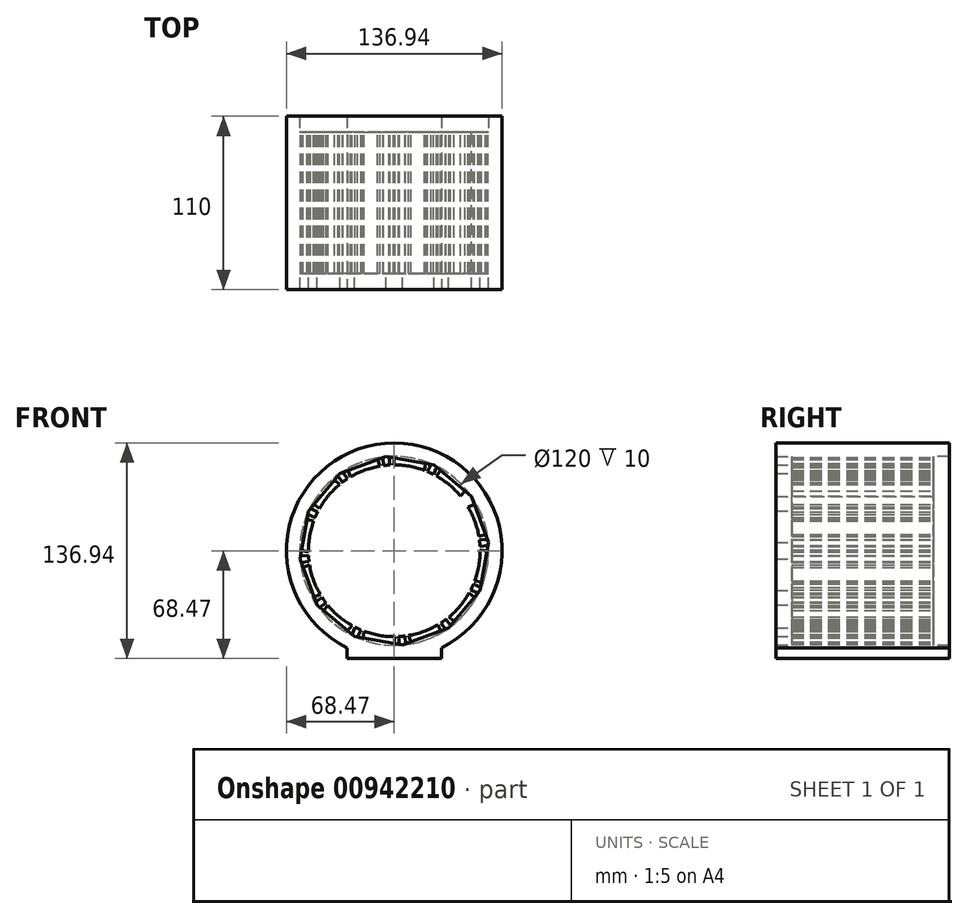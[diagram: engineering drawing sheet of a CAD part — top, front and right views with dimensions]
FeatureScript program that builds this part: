
annotation { "Feature Type Name" : "Feature", "Feature Type Description" : "" }
export const myFeature = defineFeature(function(context is Context, id is Id, definition is map)
    precondition{}
    {
        {
            var Q0;
            Q0=qCreatedBy(makeId("Front.planeOp"),FACE);
            var sketch = newSketch(context, id + "F0", { "sketchPlane" : qUnion([Q0])});
            skCircle(sketch, "E0.cCircle", {"center": v(0, 0) * mm, "radius": 60 * mm, "construction": true});
            skLineSegment(sketch, "E0.0", {"start": v(-54.41, 25.28) * mm, "end": v(-34.48, 49.1) * mm});
            skLineSegment(sketch, "E0.1", {"start": v(-34.48, 49.1) * mm, "end": v(-5.3, 59.76) * mm});
            skLineSegment(sketch, "E0.2", {"start": v(-5.3, 59.76) * mm, "end": v(25.28, 54.41) * mm});
            skLineSegment(sketch, "E0.3", {"start": v(25.28, 54.41) * mm, "end": v(49.1, 34.48) * mm});
            skLineSegment(sketch, "E0.4", {"start": v(49.1, 34.48) * mm, "end": v(59.76, 5.3) * mm});
            skLineSegment(sketch, "E0.5", {"start": v(59.76, 5.3) * mm, "end": v(54.41, -25.28) * mm});
            skLineSegment(sketch, "E0.6", {"start": v(54.41, -25.28) * mm, "end": v(34.48, -49.1) * mm});
            skLineSegment(sketch, "E0.7", {"start": v(34.48, -49.1) * mm, "end": v(5.3, -59.76) * mm});
            skLineSegment(sketch, "E0.8", {"start": v(5.3, -59.76) * mm, "end": v(-25.28, -54.41) * mm});
            skLineSegment(sketch, "E0.9", {"start": v(-25.28, -54.41) * mm, "end": v(-49.1, -34.48) * mm});
            skLineSegment(sketch, "E0.10", {"start": v(-49.1, -34.48) * mm, "end": v(-59.76, -5.3) * mm});
            skLineSegment(sketch, "E0.11", {"start": v(-59.76, -5.3) * mm, "end": v(-54.41, 25.28) * mm});
            skLineSegment(sketch, "E1", {"start": v(-34.2, 41.65) * mm, "end": v(-38.03, 44.86) * mm});
            skLineSegment(sketch, "E2", {"start": v(-47.03, 26.32) * mm, "end": v(-50.86, 29.52) * mm});
            skLineSegment(sketch, "E3", {"start": v(-34.2, 41.65) * mm, "end": v(-47.03, 26.32) * mm});
            skLineSegment(sketch, "E4", {"start": v(-4.76, 53.53) * mm, "end": v(5.3, -59.76) * mm, "construction": true});
            skLineSegment(sketch, "E5", {"start": v(-50.44, 18.98) * mm, "end": v(-55.37, 19.84) * mm});
            skLineSegment(sketch, "E6", {"start": v(-53.89, -0.73) * mm, "end": v(-58.81, 0.14) * mm});
            skLineSegment(sketch, "E7", {"start": v(-53.17, -8.79) * mm, "end": v(-57.87, -10.5) * mm});
            skLineSegment(sketch, "E8", {"start": v(-46.3, -27.57) * mm, "end": v(-51, -29.29) * mm});
            skLineSegment(sketch, "E9", {"start": v(-41.65, -34.2) * mm, "end": v(-44.86, -38.03) * mm});
            skLineSegment(sketch, "E10", {"start": v(-26.32, -47.03) * mm, "end": v(-29.52, -50.86) * mm});
            skLineSegment(sketch, "E11", {"start": v(-18.98, -50.44) * mm, "end": v(-19.84, -55.37) * mm});
            skLineSegment(sketch, "E12", {"start": v(0.73, -53.89) * mm, "end": v(-0.14, -58.81) * mm});
            skLineSegment(sketch, "E13", {"start": v(-8.79, 53.17) * mm, "end": v(-10.5, 57.87) * mm});
            skLineSegment(sketch, "E14", {"start": v(-27.57, 46.3) * mm, "end": v(-29.29, 51) * mm});
            skLineSegment(sketch, "E15.MirrorCS", {"start": v(-0.73, 53.89) * mm, "end": v(0.14, 58.81) * mm});
            skLineSegment(sketch, "E16.MirrorCS", {"start": v(18.98, 50.44) * mm, "end": v(19.84, 55.37) * mm});
            skLineSegment(sketch, "E17.MirrorCS", {"start": v(26.32, 47.03) * mm, "end": v(29.52, 50.86) * mm});
            skLineSegment(sketch, "E18.MirrorCS", {"start": v(26.32, 47.03) * mm, "end": v(41.65, 34.2) * mm});
            skLineSegment(sketch, "E19.MirrorCS", {"start": v(41.65, 34.2) * mm, "end": v(44.86, 38.03) * mm});
            skLineSegment(sketch, "E20.MirrorCS", {"start": v(46.3, 27.57) * mm, "end": v(51, 29.29) * mm});
            skLineSegment(sketch, "E21.MirrorCS", {"start": v(53.17, 8.79) * mm, "end": v(57.87, 10.5) * mm});
            skLineSegment(sketch, "E22.MirrorCS", {"start": v(53.89, 0.73) * mm, "end": v(58.81, -0.14) * mm});
            skLineSegment(sketch, "E23.MirrorCS", {"start": v(50.44, -18.98) * mm, "end": v(55.37, -19.84) * mm});
            skLineSegment(sketch, "E24.MirrorCS", {"start": v(47.03, -26.32) * mm, "end": v(50.86, -29.52) * mm});
            skLineSegment(sketch, "E25.MirrorCS", {"start": v(34.2, -41.65) * mm, "end": v(38.03, -44.86) * mm});
            skLineSegment(sketch, "E26.MirrorCS", {"start": v(27.57, -46.3) * mm, "end": v(29.29, -51) * mm});
            skLineSegment(sketch, "E27.MirrorCS", {"start": v(8.79, -53.17) * mm, "end": v(10.5, -57.87) * mm});
            skLineSegment(sketch, "E28", {"start": v(0.73, -53.89) * mm, "end": v(-18.98, -50.44) * mm});
            skLineSegment(sketch, "E29", {"start": v(-26.32, -47.03) * mm, "end": v(-41.65, -34.2) * mm});
            skLineSegment(sketch, "E30", {"start": v(-46.3, -27.57) * mm, "end": v(-53.17, -8.79) * mm});
            skLineSegment(sketch, "E31", {"start": v(-53.89, -0.73) * mm, "end": v(-50.44, 18.98) * mm});
            skLineSegment(sketch, "E32", {"start": v(-27.57, 46.3) * mm, "end": v(-8.79, 53.17) * mm});
            skPoint(sketch, "E33.MirrorCS.end.orphan", {"position": v(-0.73, 53.89) * mm});
            skPoint(sketch, "E34.MirrorCS.end.orphan", {"position": v(18.98, 50.44) * mm});
            skPoint(sketch, "E35.MirrorCS.end.orphan", {"position": v(46.3, 27.57) * mm});
            skPoint(sketch, "E36.MirrorCS.end.orphan", {"position": v(53.17, 8.79) * mm});
            skPoint(sketch, "E37.MirrorCS.end.orphan", {"position": v(53.89, 0.73) * mm});
            skPoint(sketch, "E38.MirrorCS.end.orphan", {"position": v(50.44, -18.98) * mm});
            skPoint(sketch, "E39.MirrorCS.end.orphan", {"position": v(47.03, -26.32) * mm});
            skPoint(sketch, "E40.MirrorCS.end.orphan", {"position": v(34.2, -41.65) * mm});
            skPoint(sketch, "E41.MirrorCS.end.orphan", {"position": v(27.57, -46.3) * mm});
            skPoint(sketch, "E42.MirrorCS.end.orphan", {"position": v(8.79, -53.17) * mm});
            skLineSegment(sketch, "E43", {"start": v(-0.73, 53.89) * mm, "end": v(18.98, 50.44) * mm});
            skLineSegment(sketch, "E44", {"start": v(46.3, 27.57) * mm, "end": v(53.17, 8.79) * mm});
            skLineSegment(sketch, "E45", {"start": v(53.89, 0.73) * mm, "end": v(50.44, -18.98) * mm});
            skLineSegment(sketch, "E46", {"start": v(47.03, -26.32) * mm, "end": v(34.2, -41.65) * mm});
            skLineSegment(sketch, "E47", {"start": v(27.57, -46.3) * mm, "end": v(8.79, -53.17) * mm});
            skCircle(sketch, "E48", {"center": v(0, 0) * mm, "radius": 60 * mm});
            skCircle(sketch, "E49", {"center": v(0, 0) * mm, "radius": 68.47 * mm});
            skLineSegment(sketch, "E50", {"start": v(-29.23, 45.14) * mm, "end": v(-30.88, 43.98) * mm});
            skLineSegment(sketch, "E51", {"start": v(-47.88, 24.48) * mm, "end": v(-48.73, 22.65) * mm});
            skLineSegment(sketch, "E52", {"start": v(-53.7, -2.74) * mm, "end": v(-53.53, -4.76) * mm});
            skLineSegment(sketch, "E53", {"start": v(-6.77, 53.35) * mm, "end": v(-4.76, 53.53) * mm});
            skLineSegment(sketch, "E54", {"start": v(-5.3, 59.76) * mm, "end": v(-4.76, 53.53) * mm});
            skLineSegment(sketch, "E55", {"start": v(20.81, 49.59) * mm, "end": v(22.65, 48.73) * mm});
            skLineSegment(sketch, "E56", {"start": v(42.82, 32.54) * mm, "end": v(43.98, 30.88) * mm});
            skLineSegment(sketch, "E57", {"start": v(5.3, -59.76) * mm, "end": v(4.76, -53.53) * mm});
            skLineSegment(sketch, "E58", {"start": v(-42.82, -32.54) * mm, "end": v(-43.98, -30.88) * mm});
            skLineSegment(sketch, "E59", {"start": v(-43.98, -30.88) * mm, "end": v(-45.14, -29.23) * mm});
            skLineSegment(sketch, "E60", {"start": v(43.98, 30.88) * mm, "end": v(45.14, 29.23) * mm});
            skLineSegment(sketch, "E61", {"start": v(22.65, 48.73) * mm, "end": v(24.48, 47.88) * mm});
            skLineSegment(sketch, "E62", {"start": v(-4.76, 53.53) * mm, "end": v(-2.74, 53.7) * mm});
            skLineSegment(sketch, "E63", {"start": v(-30.88, 43.98) * mm, "end": v(-32.54, 42.82) * mm});
            skLineSegment(sketch, "E64", {"start": v(-48.73, 22.65) * mm, "end": v(-49.59, 20.81) * mm});
            skLineSegment(sketch, "E65", {"start": v(-47.88, 24.48) * mm, "end": v(-53.07, 26.9) * mm});
            skLineSegment(sketch, "E66.MirrorCS", {"start": v(-49.59, 20.81) * mm, "end": v(-54.77, 23.22) * mm});
            skPoint(sketch, "E67.end.orphan", {"position": v(-48.73, 22.65) * mm});
            skLineSegment(sketch, "E68", {"start": v(-53.53, -4.76) * mm, "end": v(-53.35, -6.77) * mm});
            skLineSegment(sketch, "E69", {"start": v(-53.7, -2.74) * mm, "end": v(-59.4, -3.25) * mm});
            skLineSegment(sketch, "E70.MirrorCS", {"start": v(-53.35, -6.77) * mm, "end": v(-59.05, -7.28) * mm});
            skPoint(sketch, "E71.end.orphan", {"position": v(-53.53, -4.76) * mm});
            skLineSegment(sketch, "E72", {"start": v(-45.14, -29.23) * mm, "end": v(-49.82, -32.51) * mm});
            skLineSegment(sketch, "E73.MirrorCS", {"start": v(-42.82, -32.54) * mm, "end": v(-47.5, -35.83) * mm});
            skPoint(sketch, "E74.end.orphan", {"position": v(-43.98, -30.88) * mm});
            skLineSegment(sketch, "E75", {"start": v(-32.54, 42.82) * mm, "end": v(-35.83, 47.5) * mm});
            skLineSegment(sketch, "E76.MirrorCS", {"start": v(-29.23, 45.14) * mm, "end": v(-32.51, 49.82) * mm});
            skPoint(sketch, "E77.end.orphan", {"position": v(-30.88, 43.98) * mm});
            skLineSegment(sketch, "E78", {"start": v(-6.77, 53.35) * mm, "end": v(-7.28, 59.05) * mm});
            skLineSegment(sketch, "E79.MirrorCS", {"start": v(-2.74, 53.7) * mm, "end": v(-3.25, 59.4) * mm});
            skLineSegment(sketch, "E80", {"start": v(20.81, 49.59) * mm, "end": v(23.22, 54.77) * mm});
            skLineSegment(sketch, "E81.MirrorCS", {"start": v(24.48, 47.88) * mm, "end": v(26.9, 53.07) * mm});
            skPoint(sketch, "E82.end.orphan", {"position": v(22.65, 48.73) * mm});
            skLineSegment(sketch, "E83", {"start": v(42.82, 32.54) * mm, "end": v(47.5, 35.83) * mm});
            skLineSegment(sketch, "E84.MirrorCS", {"start": v(45.14, 29.23) * mm, "end": v(49.82, 32.51) * mm});
            skPoint(sketch, "E85.end.orphan", {"position": v(43.98, 30.88) * mm});
            skLineSegment(sketch, "E86.MirrorCS", {"start": v(53.35, 6.77) * mm, "end": v(59.05, 7.28) * mm});
            skLineSegment(sketch, "E87.MirrorCS", {"start": v(53.7, 2.74) * mm, "end": v(59.4, 3.25) * mm});
            skLineSegment(sketch, "E88.MirrorCS", {"start": v(53.53, 4.76) * mm, "end": v(53.7, 2.74) * mm});
            skLineSegment(sketch, "E89.MirrorCS", {"start": v(53.35, 6.77) * mm, "end": v(53.53, 4.76) * mm});
            skLineSegment(sketch, "E90", {"start": v(-20.81, -49.59) * mm, "end": v(-22.65, -48.73) * mm});
            skLineSegment(sketch, "E91", {"start": v(-22.65, -48.73) * mm, "end": v(-26.32, -47.03) * mm});
            skLineSegment(sketch, "E92", {"start": v(59.76, 5.3) * mm, "end": v(-59.76, -5.3) * mm, "construction": true});
            skLineSegment(sketch, "E93.MirrorCS", {"start": v(6.77, -53.35) * mm, "end": v(7.28, -59.05) * mm});
            skLineSegment(sketch, "E94.MirrorCS", {"start": v(2.74, -53.7) * mm, "end": v(3.25, -59.4) * mm});
            skLineSegment(sketch, "E95.MirrorCS", {"start": v(2.74, -53.7) * mm, "end": v(4.76, -53.53) * mm});
            skLineSegment(sketch, "E96.MirrorCS", {"start": v(4.76, -53.53) * mm, "end": v(6.77, -53.35) * mm});
            skLineSegment(sketch, "E97.MirrorCS", {"start": v(-20.81, -49.59) * mm, "end": v(-23.22, -54.77) * mm});
            skLineSegment(sketch, "E98.MirrorCS", {"start": v(-24.48, -47.88) * mm, "end": v(-26.9, -53.07) * mm});
            skLineSegment(sketch, "E99", {"start": v(49.1, 34.48) * mm, "end": v(-49.1, -34.48) * mm, "construction": true});
            skLineSegment(sketch, "E100", {"start": v(-54.41, 25.28) * mm, "end": v(54.41, -25.28) * mm, "construction": true});
            skLineSegment(sketch, "E101", {"start": v(25.28, 54.41) * mm, "end": v(-25.28, -54.41) * mm, "construction": true});
            skLineSegment(sketch, "E102", {"start": v(34.48, -49.1) * mm, "end": v(-34.48, 49.1) * mm, "construction": true});
            skLineSegment(sketch, "E103.MirrorCS", {"start": v(29.23, -45.14) * mm, "end": v(32.51, -49.82) * mm});
            skLineSegment(sketch, "E104.MirrorCS", {"start": v(32.54, -42.82) * mm, "end": v(35.83, -47.5) * mm});
            skPoint(sketch, "E105.MirrorP", {"position": v(30.88, -43.98) * mm});
            skLineSegment(sketch, "E106.MirrorCS", {"start": v(30.88, -43.98) * mm, "end": v(29.23, -45.14) * mm});
            skLineSegment(sketch, "E107.MirrorCS", {"start": v(32.54, -42.82) * mm, "end": v(30.88, -43.98) * mm});
            skLineSegment(sketch, "E108.MirrorCS", {"start": v(49.59, -20.81) * mm, "end": v(54.77, -23.22) * mm});
            skLineSegment(sketch, "E109.MirrorCS", {"start": v(47.88, -24.48) * mm, "end": v(53.07, -26.9) * mm});
            skLineSegment(sketch, "E110.MirrorCS", {"start": v(48.73, -22.65) * mm, "end": v(47.88, -24.48) * mm});
            skLineSegment(sketch, "E111.MirrorCS", {"start": v(49.59, -20.81) * mm, "end": v(48.73, -22.65) * mm});
            skSolve(sketch);
        }
        {
            var Q0;
            Q0=makeQuery(id+"F0.imprint","IMPRINT",FACE,{"disambiguationData":[TD([[makeQuery(id+"F0.imprint","IMPRINT",EDGE,{"derivedFrom":sQuery(id+"F0.wireOp",EDGE,"E49")}),1.0]])]});
            var Q1;
            {var subQ0=sQuery(id+"F0.wireOp",EDGE,"E0.11");var subQ3=makeQuery(id+"F0.imprint","INTERSECT",VERTEX,{"derivedFrom":[subQ0,sQuery(id+"F0.wireOp",EDGE,"E6")]});Q1=makeQuery(id+"F0.imprint","IMPRINT",FACE,{"disambiguationData":[TD([[makeQuery(id+"F0.imprint","IMPRINT",EDGE,{"disambiguationData":[TD([[subQ3,1.0]])],"derivedFrom":subQ0}),1.0]])]});}
            var Q2;
            {var subQ0=sQuery(id+"F0.wireOp",EDGE,"E0.10");var subQ3=makeQuery(id+"F0.imprint","INTERSECT",VERTEX,{"derivedFrom":[subQ0,sQuery(id+"F0.wireOp",EDGE,"E8")]});Q2=makeQuery(id+"F0.imprint","IMPRINT",FACE,{"disambiguationData":[TD([[makeQuery(id+"F0.imprint","IMPRINT",EDGE,{"disambiguationData":[TD([[subQ3,1.0]])],"derivedFrom":subQ0}),1.0]])]});}
            var Q3;
            {var subQ0=sQuery(id+"F0.wireOp",EDGE,"E0.9");var subQ3=makeQuery(id+"F0.imprint","INTERSECT",VERTEX,{"derivedFrom":[subQ0,sQuery(id+"F0.wireOp",EDGE,"E10")]});Q3=makeQuery(id+"F0.imprint","IMPRINT",FACE,{"disambiguationData":[TD([[makeQuery(id+"F0.imprint","IMPRINT",EDGE,{"disambiguationData":[TD([[subQ3,1.0]])],"derivedFrom":subQ0}),1.0]])]});}
            var Q4;
            {var subQ0=sQuery(id+"F0.wireOp",EDGE,"E0.8");var subQ3=makeQuery(id+"F0.imprint","INTERSECT",VERTEX,{"derivedFrom":[subQ0,sQuery(id+"F0.wireOp",EDGE,"E12")]});Q4=makeQuery(id+"F0.imprint","IMPRINT",FACE,{"disambiguationData":[TD([[makeQuery(id+"F0.imprint","IMPRINT",EDGE,{"disambiguationData":[TD([[subQ3,1.0]])],"derivedFrom":subQ0}),1.0]])]});}
            var Q5;
            {var subQ0=sQuery(id+"F0.wireOp",EDGE,"E0.7");var subQ6=makeQuery(id+"F0.imprint","INTERSECT",VERTEX,{"derivedFrom":[subQ0,sQuery(id+"F0.wireOp",EDGE,"E26.MirrorCS")]});Q5=makeQuery(id+"F0.imprint","IMPRINT",FACE,{"disambiguationData":[TD([[makeQuery(id+"F0.imprint","IMPRINT",EDGE,{"disambiguationData":[TD([[subQ6,1.0]])],"derivedFrom":subQ0}),1.0]])]});}
            var Q6;
            {var subQ0=sQuery(id+"F0.wireOp",EDGE,"E0.6");var subQ3=makeQuery(id+"F0.imprint","INTERSECT",VERTEX,{"derivedFrom":[subQ0,sQuery(id+"F0.wireOp",EDGE,"E24.MirrorCS")]});Q6=makeQuery(id+"F0.imprint","IMPRINT",FACE,{"disambiguationData":[TD([[makeQuery(id+"F0.imprint","IMPRINT",EDGE,{"disambiguationData":[TD([[subQ3,1.0]])],"derivedFrom":subQ0}),1.0]])]});}
            var Q7;
            {var subQ0=sQuery(id+"F0.wireOp",EDGE,"E0.5");var subQ3=makeQuery(id+"F0.imprint","INTERSECT",VERTEX,{"derivedFrom":[subQ0,sQuery(id+"F0.wireOp",EDGE,"E22.MirrorCS")]});Q7=makeQuery(id+"F0.imprint","IMPRINT",FACE,{"disambiguationData":[TD([[makeQuery(id+"F0.imprint","IMPRINT",EDGE,{"disambiguationData":[TD([[subQ3,1.0]])],"derivedFrom":subQ0}),1.0]])]});}
            var Q8;
            {var subQ0=sQuery(id+"F0.wireOp",EDGE,"E0.0");var subQ3=makeQuery(id+"F0.imprint","INTERSECT",VERTEX,{"derivedFrom":[subQ0,sQuery(id+"F0.wireOp",EDGE,"E2")]});Q8=makeQuery(id+"F0.imprint","IMPRINT",FACE,{"disambiguationData":[TD([[makeQuery(id+"F0.imprint","IMPRINT",EDGE,{"disambiguationData":[TD([[subQ3,1.0]])],"derivedFrom":subQ0}),1.0]])]});}
            var Q9;
            {var subQ0=sQuery(id+"F0.wireOp",EDGE,"E0.1");var subQ3=makeQuery(id+"F0.imprint","INTERSECT",VERTEX,{"derivedFrom":[subQ0,sQuery(id+"F0.wireOp",EDGE,"E14")]});Q9=makeQuery(id+"F0.imprint","IMPRINT",FACE,{"disambiguationData":[TD([[makeQuery(id+"F0.imprint","IMPRINT",EDGE,{"disambiguationData":[TD([[subQ3,1.0]])],"derivedFrom":subQ0}),1.0]])]});}
            var Q10;
            {var subQ0=sQuery(id+"F0.wireOp",EDGE,"E0.2");var subQ3=makeQuery(id+"F0.imprint","INTERSECT",VERTEX,{"derivedFrom":[subQ0,sQuery(id+"F0.wireOp",EDGE,"E15.MirrorCS")]});Q10=makeQuery(id+"F0.imprint","IMPRINT",FACE,{"disambiguationData":[TD([[makeQuery(id+"F0.imprint","IMPRINT",EDGE,{"disambiguationData":[TD([[subQ3,1.0]])],"derivedFrom":subQ0}),1.0]])]});}
            var Q11;
            {var subQ0=sQuery(id+"F0.wireOp",EDGE,"E0.3");var subQ3=makeQuery(id+"F0.imprint","INTERSECT",VERTEX,{"derivedFrom":[subQ0,sQuery(id+"F0.wireOp",EDGE,"E17.MirrorCS")]});Q11=makeQuery(id+"F0.imprint","IMPRINT",FACE,{"disambiguationData":[TD([[makeQuery(id+"F0.imprint","IMPRINT",EDGE,{"disambiguationData":[TD([[subQ3,1.0]])],"derivedFrom":subQ0}),1.0]])]});}
            var Q12;
            {var subQ0=sQuery(id+"F0.wireOp",EDGE,"E0.4");var subQ3=makeQuery(id+"F0.imprint","INTERSECT",VERTEX,{"derivedFrom":[subQ0,sQuery(id+"F0.wireOp",EDGE,"E20.MirrorCS")]});Q12=makeQuery(id+"F0.imprint","IMPRINT",FACE,{"disambiguationData":[TD([[makeQuery(id+"F0.imprint","IMPRINT",EDGE,{"disambiguationData":[TD([[subQ3,1.0]])],"derivedFrom":subQ0}),1.0]])]});}
            extrude(context, id + "F1", {"entities" : qUnion([Q0, Q1, Q2, Q3, Q4, Q5, Q6, Q7, Q8, Q9, Q10, Q11, Q12]), "depth" : 100 * mm, "offsetDistance" : 25 * mm});
        }
        {
            var Q0;
            Q0=qCreatedBy(makeId("Front.planeOp"),FACE);
            var sketch = newSketch(context, id + "F2", { "sketchPlane" : qUnion([Q0])});
            skCircle(sketch, "E112", {"center": v(0, 0) * mm, "radius": 54.56 * mm});
            skSolve(sketch);
        }
        {
            var Q0;
            {var subQ0=sQuery(id+"F0.wireOp",EDGE,"E2");Q0=makeQuery(id+"F0.imprint","IMPRINT",FACE,{"disambiguationData":[TD([[makeQuery(id+"F0.imprint","IMPRINT",EDGE,{"derivedFrom":subQ0}),-1.0]])]});}
            var Q1;
            {var subQ0=sQuery(id+"F0.wireOp",EDGE,"E7");Q1=makeQuery(id+"F0.imprint","IMPRINT",FACE,{"disambiguationData":[TD([[makeQuery(id+"F0.imprint","IMPRINT",EDGE,{"derivedFrom":subQ0}),1.0]])]});}
            var Q2;
            {var subQ0=sQuery(id+"F0.wireOp",EDGE,"E15.MirrorCS");Q2=makeQuery(id+"F0.imprint","IMPRINT",FACE,{"disambiguationData":[TD([[makeQuery(id+"F0.imprint","IMPRINT",EDGE,{"derivedFrom":subQ0}),-1.0]])]});}
            var Q3;
            {var subQ0=sQuery(id+"F0.wireOp",EDGE,"E20.MirrorCS");Q3=makeQuery(id+"F0.imprint","IMPRINT",FACE,{"disambiguationData":[TD([[makeQuery(id+"F0.imprint","IMPRINT",EDGE,{"derivedFrom":subQ0}),-1.0]])]});}
            var Q4;
            {var subQ0=sQuery(id+"F0.wireOp",EDGE,"E24.MirrorCS");Q4=makeQuery(id+"F0.imprint","IMPRINT",FACE,{"disambiguationData":[TD([[makeQuery(id+"F0.imprint","IMPRINT",EDGE,{"derivedFrom":subQ0}),-1.0]])]});}
            var Q5;
            {var subQ0=sQuery(id+"F0.wireOp",EDGE,"E11");Q5=makeQuery(id+"F0.imprint","IMPRINT",FACE,{"disambiguationData":[TD([[makeQuery(id+"F0.imprint","IMPRINT",EDGE,{"derivedFrom":subQ0}),1.0]])]});}
            var Q6;
            Q6=makeQuery(id+"F0.imprint","IMPRINT",FACE,{"disambiguationData":[TD([[makeQuery(id+"F0.imprint","IMPRINT",EDGE,{"derivedFrom":sQuery(id+"F0.wireOp",EDGE,"E58")}),1.0]])]});
            var Q7;
            Q7=makeQuery(id+"F0.imprint","IMPRINT",FACE,{"disambiguationData":[TD([[makeQuery(id+"F0.imprint","IMPRINT",EDGE,{"derivedFrom":sQuery(id+"F0.wireOp",EDGE,"E51")}),-1.0]])]});
            var Q8;
            {var subQ0=sQuery(id+"F0.wireOp",EDGE,"E54");Q8=makeQuery(id+"F0.imprint","IMPRINT",FACE,{"disambiguationData":[TD([[makeQuery(id+"F0.imprint","IMPRINT",EDGE,{"derivedFrom":subQ0}),1.0]])]});}
            var Q9;
            Q9=makeQuery(id+"F0.imprint","IMPRINT",FACE,{"disambiguationData":[TD([[makeQuery(id+"F0.imprint","IMPRINT",EDGE,{"derivedFrom":sQuery(id+"F0.wireOp",EDGE,"E53")}),1.0]])]});
            var Q10;
            Q10=makeQuery(id+"F0.imprint","IMPRINT",FACE,{"disambiguationData":[TD([[makeQuery(id+"F0.imprint","IMPRINT",EDGE,{"derivedFrom":sQuery(id+"F0.wireOp",EDGE,"E56")}),1.0]])]});
            var Q11;
            {var subQ1=sQuery(id+"F0.wireOp",EDGE,"E108.MirrorCS");Q11=makeQuery(id+"F0.imprint","IMPRINT",FACE,{"disambiguationData":[TD([[makeQuery(id+"F0.imprint","IMPRINT",EDGE,{"derivedFrom":subQ1}),-1.0]])]});}
            var Q12;
            {var subQ0=sQuery(id+"F0.wireOp",EDGE,"E57");Q12=makeQuery(id+"F0.imprint","IMPRINT",FACE,{"disambiguationData":[TD([[makeQuery(id+"F0.imprint","IMPRINT",EDGE,{"derivedFrom":subQ0}),-1.0]])]});}
            var Q13;
            {var subQ0=sQuery(id+"F0.wireOp",EDGE,"E57");Q13=makeQuery(id+"F0.imprint","IMPRINT",FACE,{"disambiguationData":[TD([[makeQuery(id+"F0.imprint","IMPRINT",EDGE,{"derivedFrom":subQ0}),1.0]])]});}
            var Q14;
            Q14=makeQuery(id+"F0.imprint","IMPRINT",FACE,{"disambiguationData":[TD([[makeQuery(id+"F0.imprint","IMPRINT",EDGE,{"derivedFrom":sQuery(id+"F0.wireOp",EDGE,"E50")}),-1.0]])]});
            var Q15;
            {var subQ0=sQuery(id+"F0.wireOp",EDGE,"E13");Q15=makeQuery(id+"F0.imprint","IMPRINT",FACE,{"disambiguationData":[TD([[makeQuery(id+"F0.imprint","IMPRINT",EDGE,{"derivedFrom":subQ0}),1.0]])]});}
            var Q16;
            {var subQ0=sQuery(id+"F0.wireOp",EDGE,"E5");Q16=makeQuery(id+"F0.imprint","IMPRINT",FACE,{"disambiguationData":[TD([[makeQuery(id+"F0.imprint","IMPRINT",EDGE,{"derivedFrom":subQ0}),1.0]])]});}
            var Q17;
            Q17=makeQuery(id+"F0.imprint","IMPRINT",FACE,{"disambiguationData":[TD([[makeQuery(id+"F0.imprint","IMPRINT",EDGE,{"derivedFrom":sQuery(id+"F0.wireOp",EDGE,"E52")}),-1.0]])]});
            var Q18;
            {var subQ0=sQuery(id+"F0.wireOp",EDGE,"E9");Q18=makeQuery(id+"F0.imprint","IMPRINT",FACE,{"disambiguationData":[TD([[makeQuery(id+"F0.imprint","IMPRINT",EDGE,{"derivedFrom":subQ0}),1.0]])]});}
            var Q19;
            {var subQ0=sQuery(id+"F0.wireOp",EDGE,"E90");Q19=makeQuery(id+"F0.imprint","IMPRINT",FACE,{"disambiguationData":[TD([[makeQuery(id+"F0.imprint","IMPRINT",EDGE,{"derivedFrom":subQ0}),1.0]])]});}
            var Q20;
            {var subQ0=sQuery(id+"F0.wireOp",EDGE,"E26.MirrorCS");Q20=makeQuery(id+"F0.imprint","IMPRINT",FACE,{"disambiguationData":[TD([[makeQuery(id+"F0.imprint","IMPRINT",EDGE,{"derivedFrom":subQ0}),-1.0]])]});}
            var Q21;
            {var subQ1=sQuery(id+"F0.wireOp",EDGE,"E103.MirrorCS");Q21=makeQuery(id+"F0.imprint","IMPRINT",FACE,{"disambiguationData":[TD([[makeQuery(id+"F0.imprint","IMPRINT",EDGE,{"derivedFrom":subQ1}),1.0]])]});}
            var Q22;
            {var subQ0=sQuery(id+"F0.wireOp",EDGE,"E22.MirrorCS");Q22=makeQuery(id+"F0.imprint","IMPRINT",FACE,{"disambiguationData":[TD([[makeQuery(id+"F0.imprint","IMPRINT",EDGE,{"derivedFrom":subQ0}),-1.0]])]});}
            var Q23;
            {var subQ1=sQuery(id+"F0.wireOp",EDGE,"E86.MirrorCS");Q23=makeQuery(id+"F0.imprint","IMPRINT",FACE,{"disambiguationData":[TD([[makeQuery(id+"F0.imprint","IMPRINT",EDGE,{"derivedFrom":subQ1}),-1.0]])]});}
            var Q24;
            {var subQ0=sQuery(id+"F0.wireOp",EDGE,"E17.MirrorCS");Q24=makeQuery(id+"F0.imprint","IMPRINT",FACE,{"disambiguationData":[TD([[makeQuery(id+"F0.imprint","IMPRINT",EDGE,{"derivedFrom":subQ0}),-1.0]])]});}
            var Q25;
            Q25=makeQuery(id+"F0.imprint","IMPRINT",FACE,{"disambiguationData":[TD([[makeQuery(id+"F0.imprint","IMPRINT",EDGE,{"derivedFrom":sQuery(id+"F0.wireOp",EDGE,"E55")}),1.0]])]});
            var Q26;
            {var subQ0=sQuery(id+"F0.wireOp",EDGE,"WjSCq5x1-iQfi-JlUr-wsTn-zVT6PGVRjYhO");Q26=makeQuery(id+"F0.imprint","IMPRINT",FACE,{"disambiguationData":[TD([[makeQuery(id+"F0.imprint","IMPRINT",EDGE,{"derivedFrom":subQ0}),1.0]])]});}
            var Q27;
            {var subQ0=sQuery(id+"F0.wireOp",EDGE,"bFF6zqef-A4QD-V90v-uRr6-FdxKQi4tdd3k");Q27=makeQuery(id+"F0.imprint","IMPRINT",FACE,{"disambiguationData":[TD([[makeQuery(id+"F0.imprint","IMPRINT",EDGE,{"derivedFrom":subQ0}),-1.0]])]});}
            var Q28;
            {var subQ0=sQuery(id+"F0.wireOp",EDGE,"txfbCzC7-oX6N-bMFQ-sv6Z-U3SgZ6v7dDhM");Q28=makeQuery(id+"F0.imprint","IMPRINT",FACE,{"disambiguationData":[TD([[makeQuery(id+"F0.imprint","IMPRINT",EDGE,{"derivedFrom":subQ0}),-1.0]])]});}
            var Q29;
            {var subQ0=sQuery(id+"F0.wireOp",EDGE,"ojTrVozV-sLrb-Nlxh-RWCp-ZbDaVbEMSUa6");Q29=makeQuery(id+"F0.imprint","IMPRINT",FACE,{"disambiguationData":[TD([[makeQuery(id+"F0.imprint","IMPRINT",EDGE,{"derivedFrom":subQ0}),-1.0]])]});}
            var Q30;
            {var subQ0=sQuery(id+"F0.wireOp",EDGE,"yewtViJo-RQat-Op15-m3Ov-y0UxaskfiTuv");Q30=makeQuery(id+"F0.imprint","IMPRINT",FACE,{"disambiguationData":[TD([[makeQuery(id+"F0.imprint","IMPRINT",EDGE,{"derivedFrom":subQ0}),-1.0]])]});}
            var Q31;
            {var subQ0=sQuery(id+"F0.wireOp",EDGE,"uCAuPjh9-wF80-EGjK-Db98-g0qC19dmE83E");Q31=makeQuery(id+"F0.imprint","IMPRINT",FACE,{"disambiguationData":[TD([[makeQuery(id+"F0.imprint","IMPRINT",EDGE,{"derivedFrom":subQ0}),-1.0]])]});}
            var Q32;
            {var subQ5=sQuery(id+"F0.wireOp",EDGE,"CZ9W13s3-inZc-NrSP-9Z8h-QvjlMf9F96EH");Q32=makeQuery(id+"F0.imprint","IMPRINT",FACE,{"disambiguationData":[TD([[makeQuery(id+"F0.imprint","IMPRINT",EDGE,{"derivedFrom":subQ5}),1.0]])]});}
            var Q33;
            {var subQ9=sQuery(id+"F0.wireOp",EDGE,"E13");var subQ10=sQuery(id+"F0.wireOp",EDGE,"E0.1");var subQ11=makeQuery(id+"F0.imprint","INTERSECT",VERTEX,{"derivedFrom":[subQ10,subQ9]});Q33=makeQuery(id+"F0.imprint","IMPRINT",FACE,{"disambiguationData":[TD([[makeQuery(id+"F0.imprint","IMPRINT",EDGE,{"disambiguationData":[TD([[subQ11,1.0]])],"derivedFrom":subQ10}),-1.0]])]});}
            extrude(context, id + "F3", {"entities" : qUnion([Q0, Q1, Q2, Q3, Q4, Q5, Q6, Q7, Q8, Q9, Q10, Q11, Q12, Q13, Q14, Q15, Q16, Q17, Q18, Q19, Q20, Q21, Q22, Q23, Q24, Q25, Q26, Q27, Q28, Q29, Q30, Q31, Q32, Q33]), "operationType" : NewBodyOperationType.ADD, "depth" : 90 * mm, "offsetDistance" : 25 * mm});
        }
        {
            var Q0;
            Q0=makeQuery(id+"F0.imprint","IMPRINT",FACE,{"disambiguationData":[TD([[makeQuery(id+"F0.imprint","IMPRINT",EDGE,{"derivedFrom":sQuery(id+"F0.wireOp",EDGE,"E49")}),1.0]])]});
            extrude(context, id + "F4", {"entities" : qUnion([Q0]), "operationType" : NewBodyOperationType.ADD, "oppositeDirection" : true, "depth" : 10 * mm, "offsetDistance" : 25 * mm});
        }
        {
            var Q0;
            Q0=makeQuery(id+"F2.imprint","IMPRINT",FACE,{"disambiguationData":[TD([[makeQuery(id+"F2.imprint","IMPRINT",EDGE,{"derivedFrom":sQuery(id+"F2.wireOp",EDGE,"E112")}),1.0]])]});
            var Q1;
            Q1=makeQuery(id+"F3.opExtrude","CAP_FACE",FACE,{"disambiguationData":[OSD([sQuery(id+"F0.wireOp",EDGE,"E0.0"),sQuery(id+"F0.wireOp",EDGE,"E2"),sQuery(id+"F0.wireOp",EDGE,"E3"),sQuery(id+"F0.wireOp",EDGE,"E1")])],"isStart":false});
            extrude(context, id + "F5", {"entities" : qUnion([Q0]), "operationType" : NewBodyOperationType.REMOVE, "endBound" : BoundingType.UP_TO_SURFACE, "depth" : 25 * mm, "endBoundEntityFace" : qUnion([Q1]), "offsetDistance" : 25 * mm});
        }
        {
            var Q0;
            Q0=makeQuery(id+"F1.opExtrude","CAP_FACE",FACE,{"disambiguationData":[OSD([sQuery(id+"F0.wireOp",EDGE,"E0.0"),sQuery(id+"F0.wireOp",EDGE,"E0.1"),sQuery(id+"F0.wireOp",EDGE,"E0.2"),sQuery(id+"F0.wireOp",EDGE,"E0.3"),sQuery(id+"F0.wireOp",EDGE,"E0.4"),sQuery(id+"F0.wireOp",EDGE,"E0.5"),sQuery(id+"F0.wireOp",EDGE,"E0.6"),sQuery(id+"F0.wireOp",EDGE,"E0.7"),sQuery(id+"F0.wireOp",EDGE,"E0.8"),sQuery(id+"F0.wireOp",EDGE,"E0.9"),sQuery(id+"F0.wireOp",EDGE,"E0.10"),sQuery(id+"F0.wireOp",EDGE,"E0.11"),sQuery(id+"F0.wireOp",EDGE,"E49")])],"isStart":false});
            var sketch = newSketch(context, id + "F6", { "sketchPlane" : qUnion([Q0])});
            skLineSegment(sketch, "E113", {"start": v(0, -68.47) * mm, "end": v(30, -68.47) * mm});
            skLineSegment(sketch, "E114", {"start": v(0, -68.47) * mm, "end": v(-30, -68.47) * mm});
            skLineSegment(sketch, "E115", {"start": v(-30, -68.47) * mm, "end": v(-30, -61.55) * mm});
            skLineSegment(sketch, "E116", {"start": v(30, -68.47) * mm, "end": v(30, -61.55) * mm});
            skSolve(sketch);
        }
        {
            var Q0;
            {var subQ0=sQuery(id+"F6.wireOp",EDGE,"E114");Q0=makeQuery(id+"F6.imprint","IMPRINT",FACE,{"disambiguationData":[TD([[makeQuery(id+"F6.imprint","IMPRINT",EDGE,{"derivedFrom":subQ0}),-1.0]])]});}
            var Q1;
            {var subQ0=sQuery(id+"F6.wireOp",EDGE,"E113");Q1=makeQuery(id+"F6.imprint","IMPRINT",FACE,{"disambiguationData":[TD([[makeQuery(id+"F6.imprint","IMPRINT",EDGE,{"derivedFrom":subQ0}),1.0]])]});}
            var Q2;
            Q2=makeQuery(id+"F4.opExtrude","CAP_FACE",FACE,{"disambiguationData":[OSD([sQuery(id+"F0.wireOp",EDGE,"E48"),sQuery(id+"F0.wireOp",EDGE,"E49")])],"isStart":false});
            extrude(context, id + "F7", {"entities" : qUnion([Q0, Q1]), "operationType" : NewBodyOperationType.ADD, "endBound" : BoundingType.UP_TO_SURFACE, "oppositeDirection" : true, "depth" : 25 * mm, "endBoundEntityFace" : qUnion([Q2]), "offsetDistance" : 25 * mm});
        }
    });
